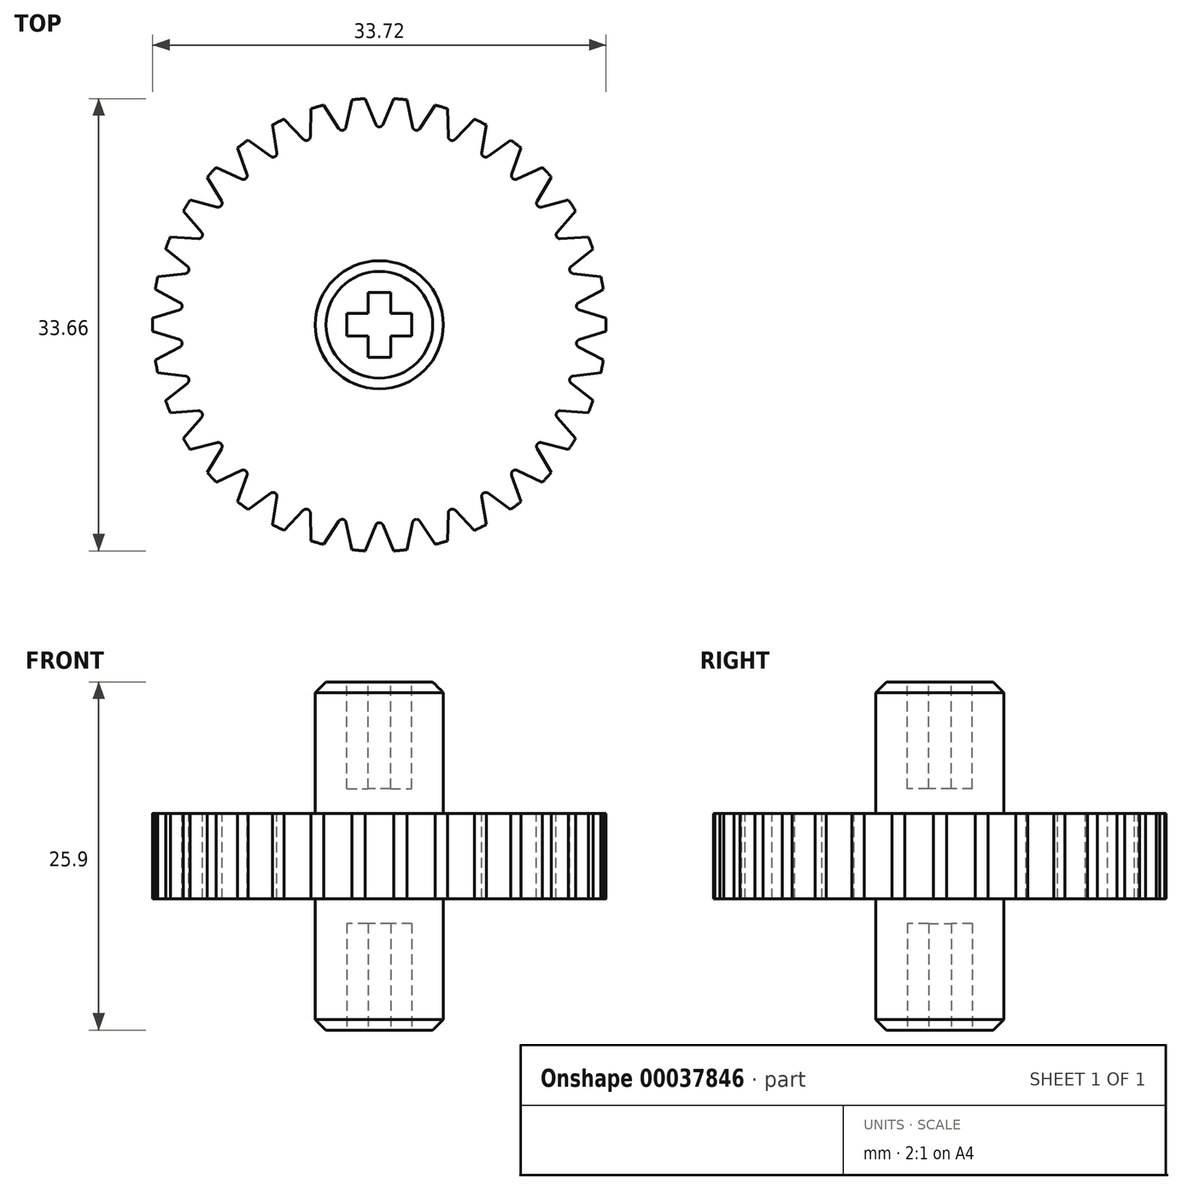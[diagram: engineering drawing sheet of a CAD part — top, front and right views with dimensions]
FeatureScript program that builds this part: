
annotation { "Feature Type Name" : "Feature", "Feature Type Description" : "" }
export const myFeature = defineFeature(function(context is Context, id is Id, definition is map)
    precondition{}
    {
        {
            var Q0;
            Q0=qCreatedBy(makeId("Top.planeOp"),FACE);
            var sketch = newSketch(context, id + "F0", { "sketchPlane" : qUnion([Q0])});
            skCircle(sketch, "E0", {"center": v(0, 0) * mm, "radius": 16.86 * mm});
            skSolve(sketch);
        }
        {
            var Q0;
            Q0 = qSketchRegion(id + "F0", true);
            extrude(context, id + "F1", {"entities" : qUnion([Q0]), "endBound" : BoundingType.SYMMETRIC, "depth" : 6.35 * mm});
        }
        {
            var Q0;
            Q0=makeQuery(id+"F1.opExtrude","CAP_FACE",FACE,{"disambiguationData":[OSD([sQuery(id+"F0.wireOp",EDGE,"E0")])],"isStart":false});
            var sketch = newSketch(context, id + "F2", { "sketchPlane" : qUnion([Q0])});
            skLineSegment(sketch, "E1", {"start": v(0, 0) * mm, "end": v(0, 16.86) * mm, "construction": true});
            skArc(sketch, "E2", {"start": v(1.07, 16.83) * mm, "mid": v(0, 16.86) * mm, "end": v(-1.07, 16.83) * mm});
            skLineSegment(sketch, "E3", {"start": v(-1.07, 16.83) * mm, "end": v(-0.28, 14.91) * mm});
            skLineSegment(sketch, "E4", {"start": v(1.07, 16.83) * mm, "end": v(0.28, 14.91) * mm});
            skArc(sketch, "E5", {"start": v(-0.28, 14.91) * mm, "mid": v(0, 14.73) * mm, "end": v(0.28, 14.91) * mm});
            skLineSegment(sketch, "E6", {"start": v(0, 0) * mm, "end": v(-0.71, 16.85) * mm, "construction": true});
            skPoint(sketch, "E7", {"position": v(-0.67, 15.87) * mm});
            skSolve(sketch);
        }
        {
            var Q0;
            Q0 = qSketchRegion(id + "F2", true);
            var Q1;
            Q1=makeQuery(id+"F1.opExtrude","CAP_FACE",FACE,{"disambiguationData":[OSD([sQuery(id+"F0.wireOp",EDGE,"E0")])],"isStart":true});
            extrude(context, id + "F3", {"entities" : qUnion([Q0]), "operationType" : NewBodyOperationType.REMOVE, "endBound" : BoundingType.UP_TO_SURFACE, "oppositeDirection" : true, "endBoundEntityFace" : qUnion([Q1]), "depth" : 25.4 * mm});
        }
        {
            var Q0;
            Q0=makeQuery(id+"F3.boolean.opBoolean","COPY",FACE,{"derivedFrom":makeQuery(id+"F3.opExtrude","SWEPT_FACE",FACE,{"disambiguationData":[OSD([sQuery(id+"F2.wireOp",EDGE,"E3")])]})});
            var Q1;
            Q1=makeQuery(id+"F3.boolean.opBoolean","COPY",FACE,{"derivedFrom":makeQuery(id+"F3.opExtrude","SWEPT_FACE",FACE,{"disambiguationData":[OSD([sQuery(id+"F2.wireOp",EDGE,"E5")])]})});
            var Q2;
            Q2=makeQuery(id+"F3.boolean.opBoolean","COPY",FACE,{"derivedFrom":makeQuery(id+"F3.opExtrude","SWEPT_FACE",FACE,{"disambiguationData":[OSD([sQuery(id+"F2.wireOp",EDGE,"E4")])]})});
            var Q3;
            Q3=makeQuery(id+"F1.opExtrude","SWEPT_FACE",FACE,{"disambiguationData":[OSD([sQuery(id+"F0.wireOp",EDGE,"E0")])]});
            circularPattern(context, id + "F4", {"faces" : qUnion([Q0, Q1, Q2]), "axis" : qUnion([Q3]), "angle" : 10.6 * degree, "instanceCount" : 34, "patternType" : PatternType.FACE});
        }
        {
            var Q0;
            Q0=qCreatedBy(makeId("Top.planeOp"),FACE);
            var sketch = newSketch(context, id + "F5", { "sketchPlane" : qUnion([Q0])});
            skCircle(sketch, "E8", {"center": v(0, 0) * mm, "radius": 4.76 * mm});
            skSolve(sketch);
        }
        {
            var Q0;
            Q0 = qSketchRegion(id + "F5", true);
            extrude(context, id + "F6", {"entities" : qUnion([Q0]), "operationType" : NewBodyOperationType.ADD, "endBound" : BoundingType.SYMMETRIC, "depth" : 25.9 * mm});
        }
        {
            var Q0;
            Q0=makeQuery(id+"F6.opExtrude","CAP_EDGE",EDGE,{"disambiguationData":[OSD([sQuery(id+"F5.wireOp",EDGE,"E8")])],"isStart":false});
            var Q1;
            Q1=makeQuery(id+"F6.opExtrude","CAP_EDGE",EDGE,{"disambiguationData":[OSD([sQuery(id+"F5.wireOp",EDGE,"E8")])],"isStart":true});
            chamfer(context, id + "F7", {"entities" : qUnion([Q0, Q1]), "width" : 0.8 * mm, "tangentPropagation" : true});
        }
        {
            var Q0;
            Q0=makeQuery(id+"F6.opExtrude","CAP_FACE",FACE,{"disambiguationData":[OSD([sQuery(id+"F5.wireOp",EDGE,"E8")])],"isStart":false});
            var sketch = newSketch(context, id + "F8", { "sketchPlane" : qUnion([Q0])});
            skLineSegment(sketch, "E9.rect.bottom", {"start": v(0.84, 2.41) * mm, "end": v(-0.84, 2.41) * mm});
            skLineSegment(sketch, "E9.rect.top", {"start": v(0.84, -2.41) * mm, "end": v(-0.84, -2.41) * mm});
            skLineSegment(sketch, "E9.rect.left", {"start": v(0.84, 2.41) * mm, "end": v(0.84, -2.41) * mm});
            skLineSegment(sketch, "E9.rect.right", {"start": v(-0.84, 2.41) * mm, "end": v(-0.84, -2.41) * mm});
            skPoint(sketch, "E9.rect.middle", {"position": v(0, 0) * mm});
            skLineSegment(sketch, "E10.rect.bottom", {"start": v(-2.41, 0.84) * mm, "end": v(2.41, 0.84) * mm});
            skLineSegment(sketch, "E10.rect.top", {"start": v(-2.41, -0.84) * mm, "end": v(2.41, -0.84) * mm});
            skLineSegment(sketch, "E10.rect.left", {"start": v(-2.41, 0.84) * mm, "end": v(-2.41, -0.84) * mm});
            skLineSegment(sketch, "E10.rect.right", {"start": v(2.41, 0.84) * mm, "end": v(2.41, -0.84) * mm});
            skSolve(sketch);
        }
        {
            var Q0;
            Q0 = qSketchRegion(id + "F8", true);
            extrude(context, id + "F9", {"entities" : qUnion([Q0]), "operationType" : NewBodyOperationType.REMOVE, "oppositeDirection" : true, "depth" : 7.94 * mm});
        }
        {
            var Q0;
            Q0=makeQuery(id+"F6.opExtrude","CAP_FACE",FACE,{"disambiguationData":[OSD([sQuery(id+"F5.wireOp",EDGE,"E8")])],"isStart":true});
            var sketch = newSketch(context, id + "F10", { "sketchPlane" : qUnion([Q0])});
            skLineSegment(sketch, "E11.rect.bottom", {"start": v(2.41, 0.84) * mm, "end": v(-2.41, 0.84) * mm});
            skLineSegment(sketch, "E11.rect.top", {"start": v(2.41, -0.84) * mm, "end": v(-2.41, -0.84) * mm});
            skLineSegment(sketch, "E11.rect.left", {"start": v(2.41, 0.84) * mm, "end": v(2.41, -0.84) * mm});
            skLineSegment(sketch, "E11.rect.right", {"start": v(-2.41, 0.84) * mm, "end": v(-2.41, -0.84) * mm});
            skPoint(sketch, "E11.rect.middle", {"position": v(0, 0) * mm});
            skLineSegment(sketch, "E12.rect.bottom", {"start": v(0.84, -2.41) * mm, "end": v(-0.84, -2.41) * mm});
            skLineSegment(sketch, "E12.rect.top", {"start": v(0.84, 2.41) * mm, "end": v(-0.84, 2.41) * mm});
            skLineSegment(sketch, "E12.rect.left", {"start": v(0.84, -2.41) * mm, "end": v(0.84, 2.41) * mm});
            skLineSegment(sketch, "E12.rect.right", {"start": v(-0.84, -2.41) * mm, "end": v(-0.84, 2.41) * mm});
            skSolve(sketch);
        }
        {
            var Q0;
            Q0 = qSketchRegion(id + "F10", true);
            extrude(context, id + "F11", {"entities" : qUnion([Q0]), "operationType" : NewBodyOperationType.REMOVE, "oppositeDirection" : true, "depth" : 7.94 * mm});
        }
    });
